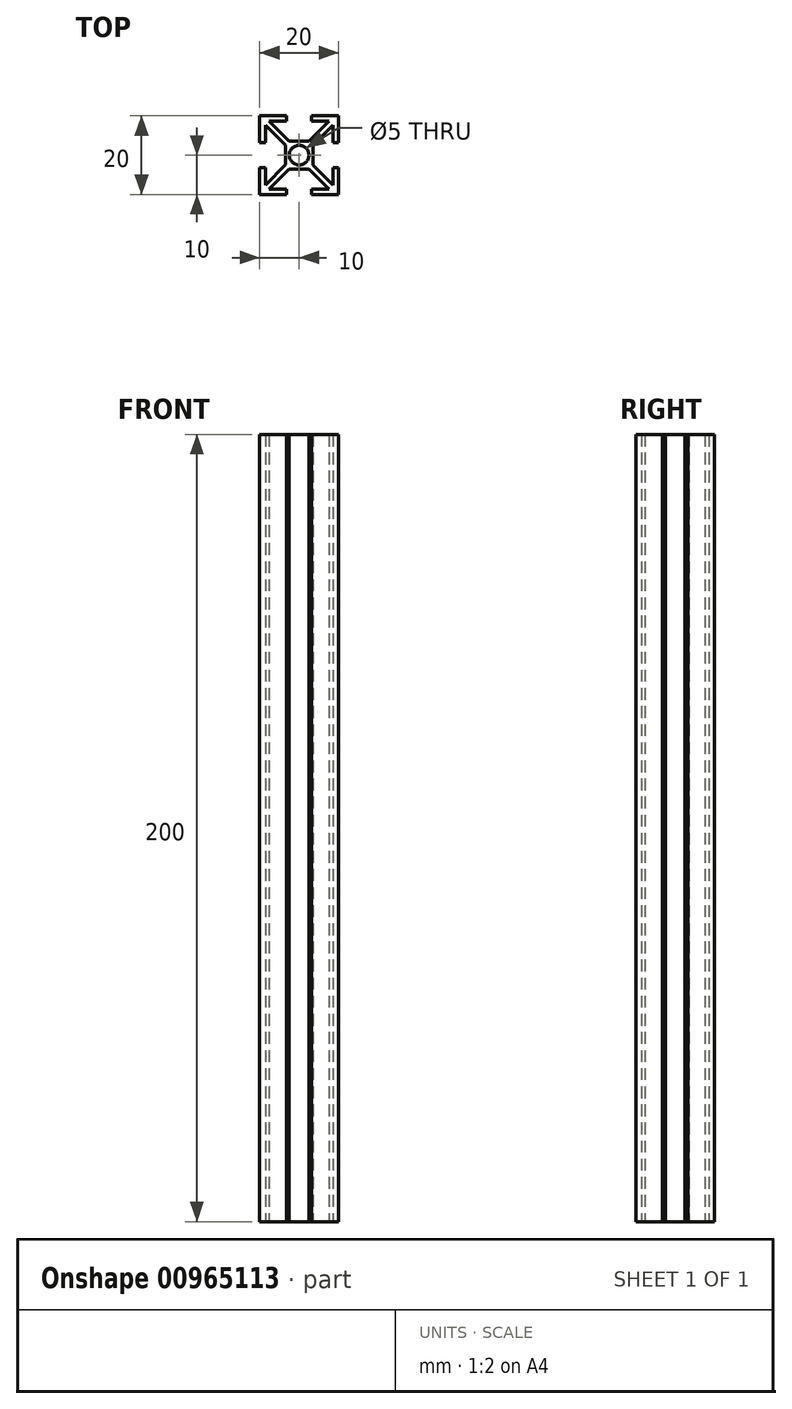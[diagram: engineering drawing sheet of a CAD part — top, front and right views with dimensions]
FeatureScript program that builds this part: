
annotation { "Feature Type Name" : "Feature", "Feature Type Description" : "" }
export const myFeature = defineFeature(function(context is Context, id is Id, definition is map)
    precondition{}
    {
        {
            var Q0;
            Q0=qCreatedBy(makeId("Top.planeOp"),FACE);
            var sketch = newSketch(context, id + "F0", { "sketchPlane" : qUnion([Q0])});
            skCircle(sketch, "E0", {"center": v(10, 10) * mm, "radius": 2.5 * mm});
            skLineSegment(sketch, "E1", {"start": v(0, 0) * mm, "end": v(10, 10) * mm, "construction": true});
            skLineSegment(sketch, "E2", {"start": v(1.4, 2.39) * mm, "end": v(1.4, 6.8) * mm});
            skLineSegment(sketch, "E3", {"start": v(1.4, 6.8) * mm, "end": v(0, 6.8) * mm});
            skLineSegment(sketch, "E4", {"start": v(0, 6.8) * mm, "end": v(0, 0) * mm});
            skLineSegment(sketch, "E5", {"start": v(7.49, 6.5) * mm, "end": v(2.39, 1.4) * mm});
            skLineSegment(sketch, "E6", {"start": v(2.39, 1.4) * mm, "end": v(6.8, 1.4) * mm});
            skLineSegment(sketch, "E7", {"start": v(6.8, 1.4) * mm, "end": v(6.8, 0) * mm});
            skLineSegment(sketch, "E8", {"start": v(6.8, 0) * mm, "end": v(0, 0) * mm});
            skLineSegment(sketch, "E9", {"start": v(10, 10) * mm, "end": v(20, 20) * mm, "construction": true});
            skLineSegment(sketch, "E10", {"start": v(10, 10) * mm, "end": v(0, 20) * mm, "construction": true});
            skLineSegment(sketch, "E11", {"start": v(10, 10) * mm, "end": v(20, 0) * mm, "construction": true});
            skLineSegment(sketch, "E12", {"start": v(1.4, 17.61) * mm, "end": v(6.5, 12.51) * mm});
            skLineSegment(sketch, "E13", {"start": v(1.4, 17.61) * mm, "end": v(1.4, 13.2) * mm});
            skLineSegment(sketch, "E14", {"start": v(1.4, 13.2) * mm, "end": v(0, 13.2) * mm});
            skLineSegment(sketch, "E15", {"start": v(0, 13.2) * mm, "end": v(0, 20) * mm});
            skLineSegment(sketch, "E16", {"start": v(7.49, 13.5) * mm, "end": v(2.39, 18.6) * mm});
            skLineSegment(sketch, "E17", {"start": v(2.39, 18.6) * mm, "end": v(6.8, 18.6) * mm});
            skLineSegment(sketch, "E18", {"start": v(6.8, 18.6) * mm, "end": v(6.8, 20) * mm});
            skLineSegment(sketch, "E19", {"start": v(6.8, 20) * mm, "end": v(0, 20) * mm});
            skLineSegment(sketch, "E20", {"start": v(12.51, 13.5) * mm, "end": v(17.61, 18.6) * mm});
            skLineSegment(sketch, "E21", {"start": v(17.61, 18.6) * mm, "end": v(13.2, 18.6) * mm});
            skLineSegment(sketch, "E22", {"start": v(13.2, 18.6) * mm, "end": v(13.2, 20) * mm});
            skLineSegment(sketch, "E23", {"start": v(13.2, 20) * mm, "end": v(20, 20) * mm});
            skLineSegment(sketch, "E24", {"start": v(13.5, 12.51) * mm, "end": v(18.6, 17.61) * mm});
            skLineSegment(sketch, "E25", {"start": v(18.6, 17.61) * mm, "end": v(18.6, 13.2) * mm});
            skLineSegment(sketch, "E26", {"start": v(18.6, 13.2) * mm, "end": v(20, 13.2) * mm});
            skLineSegment(sketch, "E27", {"start": v(20, 13.2) * mm, "end": v(20, 20) * mm});
            skLineSegment(sketch, "E28", {"start": v(18.6, 2.39) * mm, "end": v(18.6, 6.8) * mm});
            skLineSegment(sketch, "E29", {"start": v(18.6, 6.8) * mm, "end": v(20, 6.8) * mm});
            skLineSegment(sketch, "E30", {"start": v(20, 6.8) * mm, "end": v(20, 0) * mm});
            skLineSegment(sketch, "E31", {"start": v(12.51, 6.5) * mm, "end": v(17.61, 1.4) * mm});
            skLineSegment(sketch, "E32", {"start": v(17.61, 1.4) * mm, "end": v(13.2, 1.4) * mm});
            skLineSegment(sketch, "E33", {"start": v(13.2, 1.4) * mm, "end": v(13.2, 0) * mm});
            skLineSegment(sketch, "E34", {"start": v(13.2, 0) * mm, "end": v(20, 0) * mm});
            skLineSegment(sketch, "E35", {"start": v(12.51, 6.5) * mm, "end": v(7.49, 6.5) * mm});
            skLineSegment(sketch, "E36", {"start": v(7.49, 13.5) * mm, "end": v(12.51, 13.5) * mm});
            skLineSegment(sketch, "E37", {"start": v(10, 10) * mm, "end": v(10, 0) * mm, "construction": true});
            skLineSegment(sketch, "E38", {"start": v(10, 10) * mm, "end": v(18.77, 10) * mm, "construction": true});
            skLineSegment(sketch, "E39", {"start": v(10, 10) * mm, "end": v(10, 20.74) * mm, "construction": true});
            skLineSegment(sketch, "E40", {"start": v(10, 10) * mm, "end": v(0, 10) * mm, "construction": true});
            skLineSegment(sketch, "E41.bottom", {"start": v(0, 0) * mm, "end": v(20, 0) * mm, "construction": true});
            skLineSegment(sketch, "E41.top", {"start": v(0, 20) * mm, "end": v(20, 20) * mm, "construction": true});
            skLineSegment(sketch, "E41.left", {"start": v(0, 0) * mm, "end": v(0, 20) * mm, "construction": true});
            skLineSegment(sketch, "E41.right", {"start": v(20, 0) * mm, "end": v(20, 20) * mm, "construction": true});
            skLineSegment(sketch, "E42", {"start": v(18.6, 2.39) * mm, "end": v(13.5, 7.49) * mm});
            skLineSegment(sketch, "E43", {"start": v(13.5, 7.49) * mm, "end": v(13.5, 12.51) * mm});
            skLineSegment(sketch, "E44", {"start": v(1.4, 2.39) * mm, "end": v(6.5, 7.62) * mm});
            skLineSegment(sketch, "E45", {"start": v(6.5, 7.62) * mm, "end": v(6.5, 12.51) * mm});
            skSolve(sketch);
        }
        {
            var Q0;
            Q0=makeQuery(id+"F0.imprint","IMPRINT",FACE,{"disambiguationData":[TD([[makeQuery(id+"F0.imprint","IMPRINT",EDGE,{"derivedFrom":sQuery(id+"F0.wireOp",EDGE,"E0")}),-1.0]])]});
            extrude(context, id + "F1", {"entities" : qUnion([Q0]), "depth" : 200 * mm, "offsetDistance" : 25 * mm});
        }
    });
